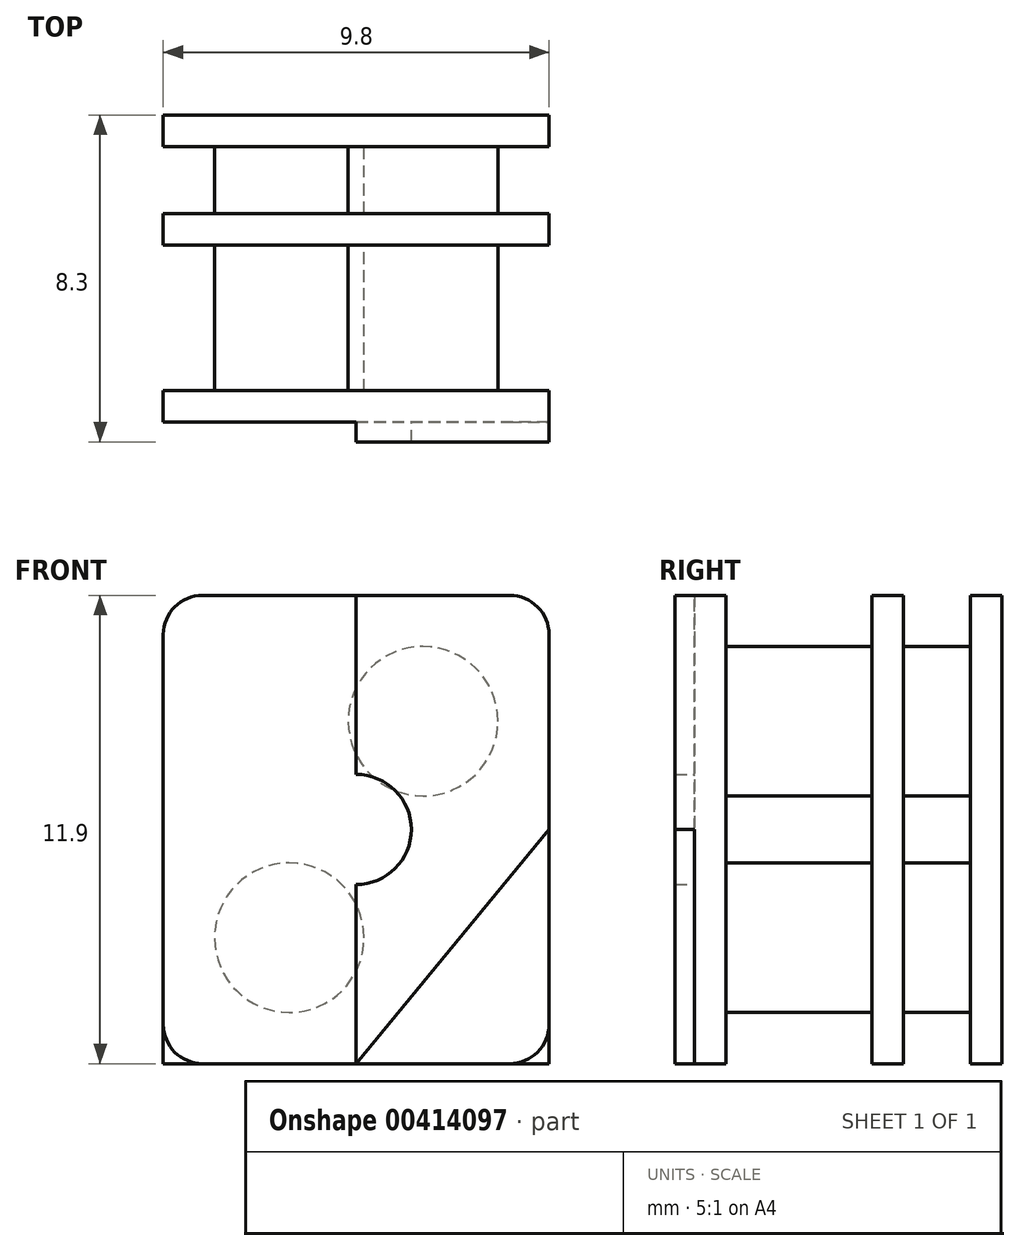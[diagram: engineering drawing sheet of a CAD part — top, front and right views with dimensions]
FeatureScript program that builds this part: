
annotation { "Feature Type Name" : "Feature", "Feature Type Description" : "" }
export const myFeature = defineFeature(function(context is Context, id is Id, definition is map)
    precondition{}
    {
        {
            var Q0;
            Q0=qCreatedBy(makeId("Front.planeOp"),FACE);
            var sketch = newSketch(context, id + "F0", { "sketchPlane" : qUnion([Q0])});
            skLineSegment(sketch, "E0.bottom", {"start": v(4.9, 5.95) * mm, "end": v(-4.9, 5.95) * mm});
            skLineSegment(sketch, "E0.top", {"start": v(4.9, -5.95) * mm, "end": v(-4.9, -5.95) * mm});
            skLineSegment(sketch, "E0.left", {"start": v(4.9, 5.95) * mm, "end": v(4.9, -5.95) * mm});
            skLineSegment(sketch, "E0.right", {"start": v(-4.9, 5.95) * mm, "end": v(-4.9, -5.95) * mm});
            skPoint(sketch, "E0.middle", {"position": v(0, 0) * mm});
            skSolve(sketch);
        }
        {
            var Q0;
            Q0=makeQuery(id+"F0.imprint","IMPRINT",FACE,{"disambiguationData":[TD([[makeQuery(id+"F0.imprint","IMPRINT",EDGE,{"derivedFrom":sQuery(id+"F0.wireOp",EDGE,"E0.bottom")}),1.0]])]});
            extrude(context, id + "F1", {"entities" : qUnion([Q0]), "depth" : .8 * mm});
        }
        {
            var Q0;
            Q0=makeQuery(id+"F1.opExtrude","CAP_FACE",FACE,{"disambiguationData":[OSD([sQuery(id+"F0.wireOp",EDGE,"E0.bottom"),sQuery(id+"F0.wireOp",EDGE,"E0.top"),sQuery(id+"F0.wireOp",EDGE,"E0.left"),sQuery(id+"F0.wireOp",EDGE,"E0.right")])],"isStart":false});
            var sketch = newSketch(context, id + "F2", { "sketchPlane" : qUnion([Q0])});
            skCircle(sketch, "E1", {"center": v(-1.7, -2.75) * mm, "radius": 1.9 * mm});
            skPoint(sketch, "E2.orphan", {"position": v(0.2, -0.85) * mm});
            skPoint(sketch, "E3.end.orphan", {"position": v(-3.6, -5.95) * mm});
            skPoint(sketch, "E4.end.orphan", {"position": v(-3.6, -4.65) * mm});
            skSolve(sketch);
        }
        {
            var Q0;
            Q0=makeQuery(id+"F1.opExtrude","CAP_FACE",FACE,{"disambiguationData":[OSD([sQuery(id+"F0.wireOp",EDGE,"E0.bottom"),sQuery(id+"F0.wireOp",EDGE,"E0.top"),sQuery(id+"F0.wireOp",EDGE,"E0.left"),sQuery(id+"F0.wireOp",EDGE,"E0.right")])],"isStart":true});
            var sketch = newSketch(context, id + "F3", { "sketchPlane" : qUnion([Q0])});
            skLineSegment(sketch, "E5.bottom", {"start": v(-4.9, 5.95) * mm, "end": v(-3.6, 5.95) * mm});
            skLineSegment(sketch, "E5.left", {"start": v(-4.9, 5.95) * mm, "end": v(-4.9, 4.65) * mm});
            skCircle(sketch, "E6", {"center": v(-1.7, 2.75) * mm, "radius": 1.9 * mm});
            skPoint(sketch, "E7.orphan", {"position": v(0.2, 0.85) * mm});
            skPoint(sketch, "E5.right.end.orphan", {"position": v(-3.6, 4.65) * mm});
            skSolve(sketch);
        }
        {
            var Q0;
            Q0=makeQuery(id+"F2.imprint","IMPRINT",FACE,{"disambiguationData":[TD([[makeQuery(id+"F2.imprint","IMPRINT",EDGE,{"derivedFrom":sQuery(id+"F2.wireOp",EDGE,"E1")}),1.0]])]});
            extrude(context, id + "F4", {"entities" : qUnion([Q0]), "operationType" : NewBodyOperationType.ADD, "depth" : 6.9 * mm});
        }
        {
            var Q0;
            Q0=makeQuery(id+"F3.imprint","IMPRINT",FACE,{"disambiguationData":[TD([[makeQuery(id+"F3.imprint","IMPRINT",EDGE,{"derivedFrom":sQuery(id+"F3.wireOp",EDGE,"E6")}),1.0]])]});
            extrude(context, id + "F5", {"entities" : qUnion([Q0]), "operationType" : NewBodyOperationType.ADD, "oppositeDirection" : true, "depth" : (.8 + 6.9) * mm});
        }
        {
            var Q0;
            Q0=makeQuery(id+"F1.opExtrude","CAP_FACE",FACE,{"disambiguationData":[OSD([sQuery(id+"F0.wireOp",EDGE,"E0.bottom"),sQuery(id+"F0.wireOp",EDGE,"E0.top"),sQuery(id+"F0.wireOp",EDGE,"E0.left"),sQuery(id+"F0.wireOp",EDGE,"E0.right")])],"isStart":false});
            var sketch = newSketch(context, id + "F6", { "sketchPlane" : qUnion([Q0])});
            skLineSegment(sketch, "E8.bottom", {"start": v(-4.9, -5.95) * mm, "end": v(4.9, -5.95) * mm});
            skLineSegment(sketch, "E8.top", {"start": v(-4.9, -5.42) * mm, "end": v(4.9, -5.42) * mm});
            skLineSegment(sketch, "E8.left", {"start": v(-4.9, -5.95) * mm, "end": v(-4.9, -5.42) * mm});
            skLineSegment(sketch, "E8.right", {"start": v(4.9, -5.95) * mm, "end": v(4.9, -5.42) * mm});
            skSolve(sketch);
        }
        {
            var Q0;
            Q0=makeQuery(id+"F6.imprint","IMPRINT",FACE,{"disambiguationData":[TD([[makeQuery(id+"F6.imprint","IMPRINT",EDGE,{"derivedFrom":sQuery(id+"F6.wireOp",EDGE,"E8.bottom")}),-1.0]])]});
            extrude(context, id + "F7", {"entities" : qUnion([Q0]), "operationType" : NewBodyOperationType.ADD, "depth" : 25.4 * mm});
        }
        {
            var Q0;
            Q0=makeQuery(id+"F7.opExtrude","SWEPT_FACE",FACE,{"disambiguationData":[OSD([sQuery(id+"F6.wireOp",EDGE,"E8.top")])]});
            var sketch = newSketch(context, id + "F8", { "sketchPlane" : qUnion([Q0])});
            skLineSegment(sketch, "E9.bottom", {"start": v(4.9, -0.8) * mm, "end": v(-4.9, -0.8) * mm});
            skLineSegment(sketch, "E9.top", {"start": v(4.9, -2.5) * mm, "end": v(-4.9, -2.5) * mm});
            skLineSegment(sketch, "E9.left", {"start": v(4.9, -0.8) * mm, "end": v(4.9, -2.5) * mm});
            skLineSegment(sketch, "E9.right", {"start": v(-4.9, -0.8) * mm, "end": v(-4.9, -2.5) * mm});
            skLineSegment(sketch, "E10.top", {"start": v(4.9, -3.3) * mm, "end": v(-4.9, -3.3) * mm});
            skLineSegment(sketch, "E10.left", {"start": v(4.9, -2.5) * mm, "end": v(4.9, -3.3) * mm});
            skLineSegment(sketch, "E10.right", {"start": v(-4.9, -2.5) * mm, "end": v(-4.9, -3.3) * mm});
            skLineSegment(sketch, "E11.top", {"start": v(4.9, -7) * mm, "end": v(-4.9, -7) * mm});
            skLineSegment(sketch, "E11.left", {"start": v(4.9, -3.3) * mm, "end": v(4.9, -7) * mm});
            skLineSegment(sketch, "E11.right", {"start": v(-4.9, -3.3) * mm, "end": v(-4.9, -7) * mm});
            skLineSegment(sketch, "E12.top", {"start": v(4.9, -7.8) * mm, "end": v(-4.9, -7.8) * mm});
            skLineSegment(sketch, "E12.left", {"start": v(4.9, -7) * mm, "end": v(4.9, -7.8) * mm});
            skLineSegment(sketch, "E12.right", {"start": v(-4.9, -7) * mm, "end": v(-4.9, -7.8) * mm});
            skSolve(sketch);
        }
        {
            var Q0;
            Q0=makeQuery(id+"F8.imprint","IMPRINT",FACE,{"disambiguationData":[TD([[makeQuery(id+"F8.imprint","IMPRINT",EDGE,{"derivedFrom":sQuery(id+"F8.wireOp",EDGE,"E9.top")}),1.0]])]});
            var Q1;
            Q1=makeQuery(id+"F8.imprint","IMPRINT",FACE,{"disambiguationData":[TD([[makeQuery(id+"F8.imprint","IMPRINT",EDGE,{"derivedFrom":sQuery(id+"F8.wireOp",EDGE,"E11.top")}),1.0]])]});
            extrude(context, id + "F9", {"entities" : qUnion([Q0, Q1]), "operationType" : NewBodyOperationType.ADD, "depth" : 11.37 * mm});
        }
        {
            var Q0;
            {var subQ2=sQuery(id+"F6.wireOp",EDGE,"E8.top");Q0=makeQuery(id+"F9.boolean.opBoolean","SPLIT",FACE,{"disambiguationData":[TD([makeQuery(id+"F9.opExtrude","SWEPT_FACE",FACE,{"disambiguationData":[OSD([sQuery(id+"F8.wireOp",EDGE,"E12.top")])]})])],"derivedFrom":makeQuery(id+"F7.opExtrude","SWEPT_FACE",FACE,{"disambiguationData":[OSD([subQ2])]})});}
            var Q1;
            Q1=makeQuery(id+"F9.boolean.opBoolean","SPLIT",FACE,{"disambiguationData":[TD([makeQuery(id+"F9.opExtrude","SWEPT_FACE",FACE,{"disambiguationData":[OSD([sQuery(id+"F8.wireOp",EDGE,"E10.top")])]})])],"derivedFrom":makeQuery(id+"F7.opExtrude","SWEPT_FACE",FACE,{"disambiguationData":[OSD([sQuery(id+"F6.wireOp",EDGE,"E8.top")])]})});
            var Q2;
            Q2=makeQuery(id+"F9.boolean.opBoolean","SPLIT",FACE,{"disambiguationData":[TD([makeQuery(id+"F9.opExtrude","SWEPT_FACE",FACE,{"disambiguationData":[OSD([sQuery(id+"F8.wireOp",EDGE,"E9.top")])]})])],"derivedFrom":makeQuery(id+"F7.opExtrude","SWEPT_FACE",FACE,{"disambiguationData":[OSD([sQuery(id+"F6.wireOp",EDGE,"E8.top")])]})});
            extrude(context, id + "F10", {"entities" : qUnion([Q0, Q1, Q2]), "operationType" : NewBodyOperationType.REMOVE, "oppositeDirection" : true, "depth" : 25.4 * mm});
        }
        {
            var Q0;
            Q0=makeQuery(id+"F9.opExtrude","CAP_EDGE",EDGE,{"disambiguationData":[OSD([sQuery(id+"F8.wireOp",EDGE,"E12.right")])],"isStart":false});
            var Q1;
            Q1=makeQuery(id+"F9.opExtrude","CAP_EDGE",EDGE,{"disambiguationData":[OSD([sQuery(id+"F8.wireOp",EDGE,"E10.right")])],"isStart":false});
            var Q2;
            Q2=makeQuery(id+"F1.opExtrude","SWEPT_EDGE",EDGE,{"disambiguationData":[OSD([sQuery(id+"F0.wireOp",EDGE,"E0.bottom"),sQuery(id+"F0.wireOp",EDGE,"E0.right")])]});
            var Q3;
            {var subQ0=sQuery(id+"F0.wireOp",EDGE,"E0.right");var subQ1=sQuery(id+"F0.wireOp",EDGE,"E0.top");var subQ2=sQuery(id+"F6.wireOp",EDGE,"E8.top");var subQ5=sQuery(id+"F6.wireOp",EDGE,"E8.bottom");var subQ6=sQuery(id+"F6.wireOp",EDGE,"E8.left");Q3=makeQuery(id+"F10.boolean.opBoolean","SPLIT",EDGE,{"disambiguationData":[TD([makeQuery(id+"F10.opExtrude","SWEPT_FACE",FACE,{"disambiguationData":[OSD([subQ2]),TDD([makeQuery(id+"F7.opExtrude","CAP_EDGE",EDGE,{"disambiguationData":[OSD([subQ2])],"isStart":true})])]})])],"derivedFrom":makeQuery(id+"F7.boolean.opBoolean","MERGE",EDGE,{"derivedFrom":[makeQuery(id+"F1.opExtrude","SWEPT_EDGE",EDGE,{"disambiguationData":[OSD([subQ1,subQ0])]}),makeQuery(id+"F7.opExtrude","SWEPT_EDGE",EDGE,{"disambiguationData":[OSD([subQ5,subQ6])]})]})});}
            var Q4;
            {var subQ0=sQuery(id+"F6.wireOp",EDGE,"E8.bottom");var subQ1=sQuery(id+"F6.wireOp",EDGE,"E8.left");var subQ2=sQuery(id+"F8.wireOp",EDGE,"E9.top");var subQ3=sQuery(id+"F0.wireOp",EDGE,"E0.right");var subQ5=sQuery(id+"F0.wireOp",EDGE,"E0.top");Q4=makeQuery(id+"F10.boolean.opBoolean","SPLIT",EDGE,{"disambiguationData":[TD([makeQuery(id+"F9.opExtrude","SWEPT_FACE",FACE,{"disambiguationData":[OSD([subQ2])]})])],"derivedFrom":makeQuery(id+"F7.boolean.opBoolean","MERGE",EDGE,{"derivedFrom":[makeQuery(id+"F1.opExtrude","SWEPT_EDGE",EDGE,{"disambiguationData":[OSD([subQ5,subQ3])]}),makeQuery(id+"F7.opExtrude","SWEPT_EDGE",EDGE,{"disambiguationData":[OSD([subQ0,subQ1])]})]})});}
            var Q5;
            {var subQ0=sQuery(id+"F6.wireOp",EDGE,"E8.bottom");var subQ1=sQuery(id+"F8.wireOp",EDGE,"E11.top");var subQ2=sQuery(id+"F6.wireOp",EDGE,"E8.left");var subQ3=sQuery(id+"F0.wireOp",EDGE,"E0.right");var subQ4=sQuery(id+"F0.wireOp",EDGE,"E0.top");Q5=makeQuery(id+"F10.boolean.opBoolean","SPLIT",EDGE,{"disambiguationData":[TD([makeQuery(id+"F9.opExtrude","SWEPT_FACE",FACE,{"disambiguationData":[OSD([subQ1])]})])],"derivedFrom":makeQuery(id+"F7.boolean.opBoolean","MERGE",EDGE,{"derivedFrom":[makeQuery(id+"F1.opExtrude","SWEPT_EDGE",EDGE,{"disambiguationData":[OSD([subQ4,subQ3])]}),makeQuery(id+"F7.opExtrude","SWEPT_EDGE",EDGE,{"disambiguationData":[OSD([subQ0,subQ2])]})]})});}
            var Q6;
            Q6=makeQuery(id+"F9.opExtrude","CAP_EDGE",EDGE,{"disambiguationData":[OSD([sQuery(id+"F8.wireOp",EDGE,"E12.left")])],"isStart":false});
            var Q7;
            Q7=makeQuery(id+"F9.opExtrude","CAP_EDGE",EDGE,{"disambiguationData":[OSD([sQuery(id+"F8.wireOp",EDGE,"E10.left")])],"isStart":false});
            var Q8;
            Q8=makeQuery(id+"F1.opExtrude","SWEPT_EDGE",EDGE,{"disambiguationData":[OSD([sQuery(id+"F0.wireOp",EDGE,"E0.bottom"),sQuery(id+"F0.wireOp",EDGE,"E0.left")])]});
            var Q9;
            {var subQ0=sQuery(id+"F0.wireOp",EDGE,"E0.left");var subQ1=sQuery(id+"F0.wireOp",EDGE,"E0.top");var subQ2=sQuery(id+"F6.wireOp",EDGE,"E8.top");var subQ5=sQuery(id+"F6.wireOp",EDGE,"E8.bottom");var subQ6=sQuery(id+"F6.wireOp",EDGE,"E8.right");Q9=makeQuery(id+"F10.boolean.opBoolean","SPLIT",EDGE,{"disambiguationData":[TD([makeQuery(id+"F10.opExtrude","SWEPT_FACE",FACE,{"disambiguationData":[OSD([subQ2]),TDD([makeQuery(id+"F7.opExtrude","CAP_EDGE",EDGE,{"disambiguationData":[OSD([subQ2])],"isStart":true})])]})])],"derivedFrom":makeQuery(id+"F7.boolean.opBoolean","MERGE",EDGE,{"derivedFrom":[makeQuery(id+"F1.opExtrude","SWEPT_EDGE",EDGE,{"disambiguationData":[OSD([subQ1,subQ0])]}),makeQuery(id+"F7.opExtrude","SWEPT_EDGE",EDGE,{"disambiguationData":[OSD([subQ5,subQ6])]})]})});}
            var Q10;
            {var subQ0=sQuery(id+"F6.wireOp",EDGE,"E8.right");var subQ1=sQuery(id+"F8.wireOp",EDGE,"E9.top");var subQ3=sQuery(id+"F6.wireOp",EDGE,"E8.bottom");var subQ4=sQuery(id+"F0.wireOp",EDGE,"E0.left");var subQ5=sQuery(id+"F0.wireOp",EDGE,"E0.top");Q10=makeQuery(id+"F10.boolean.opBoolean","SPLIT",EDGE,{"disambiguationData":[TD([makeQuery(id+"F9.opExtrude","SWEPT_FACE",FACE,{"disambiguationData":[OSD([subQ1])]})])],"derivedFrom":makeQuery(id+"F7.boolean.opBoolean","MERGE",EDGE,{"derivedFrom":[makeQuery(id+"F1.opExtrude","SWEPT_EDGE",EDGE,{"disambiguationData":[OSD([subQ5,subQ4])]}),makeQuery(id+"F7.opExtrude","SWEPT_EDGE",EDGE,{"disambiguationData":[OSD([subQ3,subQ0])]})]})});}
            var Q11;
            {var subQ0=sQuery(id+"F6.wireOp",EDGE,"E8.right");var subQ1=sQuery(id+"F6.wireOp",EDGE,"E8.bottom");var subQ2=sQuery(id+"F8.wireOp",EDGE,"E11.top");var subQ3=sQuery(id+"F0.wireOp",EDGE,"E0.left");var subQ4=sQuery(id+"F0.wireOp",EDGE,"E0.top");Q11=makeQuery(id+"F10.boolean.opBoolean","SPLIT",EDGE,{"disambiguationData":[TD([makeQuery(id+"F9.opExtrude","SWEPT_FACE",FACE,{"disambiguationData":[OSD([subQ2])]})])],"derivedFrom":makeQuery(id+"F7.boolean.opBoolean","MERGE",EDGE,{"derivedFrom":[makeQuery(id+"F1.opExtrude","SWEPT_EDGE",EDGE,{"disambiguationData":[OSD([subQ4,subQ3])]}),makeQuery(id+"F7.opExtrude","SWEPT_EDGE",EDGE,{"disambiguationData":[OSD([subQ1,subQ0])]})]})});}
            fillet(context, id + "F11", {"entities" : qUnion([Q0, Q1, Q2, Q3, Q4, Q5, Q6, Q7, Q8, Q9, Q10, Q11]), "radius" : 1 * mm, "tangentPropagation" : true, "allowEdgeOverflow" : false});
        }
        {
            var Q0;
            {var subQ0=sQuery(id+"F8.wireOp",EDGE,"E12.top");Q0=makeQuery(id+"F10.boolean.opBoolean","MERGE",FACE,{"derivedFrom":[makeQuery(id+"F9.opExtrude","SWEPT_FACE",FACE,{"disambiguationData":[OSD([subQ0])]}),makeQuery(id+"F10.opExtrude","SWEPT_FACE",FACE,{"disambiguationData":[OSD([subQ0])]})]});}
            var sketch = newSketch(context, id + "F12", { "sketchPlane" : qUnion([Q0])});
            skLineSegment(sketch, "E13", {"start": v(-4.9, 0) * mm, "end": v(4.9, 0) * mm});
            skLineSegment(sketch, "E14", {"start": v(4.9, 0) * mm, "end": v(0, -5.95) * mm});
            skLineSegment(sketch, "E15", {"start": v(0, -5.95) * mm, "end": v(0, 5.95) * mm});
            skCircle(sketch, "E16", {"center": v(0, 0) * mm, "radius": 1.95 * mm});
            skCircle(sketch, "E17", {"center": v(0, 0) * mm, "radius": 1.4 * mm});
            skSolve(sketch);
        }
        {
            var Q0;
            {var subQ0=sQuery(id+"F12.wireOp",EDGE,"E16");var subQ1=sQuery(id+"F12.wireOp",EDGE,"E13");var subQ2=makeQuery(id+"F12.imprint","INTERSECT",VERTEX,{"disambiguationData":[OD(0.0)],"derivedFrom":[subQ1,subQ0]});Q0=makeQuery(id+"F12.imprint","IMPRINT",FACE,{"disambiguationData":[TD([[makeQuery(id+"F12.imprint","IMPRINT",EDGE,{"disambiguationData":[TD([[subQ2,-1.0]])],"derivedFrom":subQ1}),-1.0]])]});}
            var Q1;
            {var subQ0=sQuery(id+"F12.wireOp",EDGE,"E17");var subQ1=sQuery(id+"F12.wireOp",EDGE,"E13");var subQ2=makeQuery(id+"F12.imprint","INTERSECT",VERTEX,{"disambiguationData":[OD(1.0)],"derivedFrom":[subQ1,subQ0]});Q1=makeQuery(id+"F12.imprint","IMPRINT",FACE,{"disambiguationData":[TD([[makeQuery(id+"F12.imprint","IMPRINT",EDGE,{"disambiguationData":[TD([[subQ2,-1.0]])],"derivedFrom":subQ1}),1.0]])]});}
            var Q2;
            {var subQ0=sQuery(id+"F12.wireOp",EDGE,"E16");var subQ1=sQuery(id+"F12.wireOp",EDGE,"E13");var subQ2=makeQuery(id+"F12.imprint","INTERSECT",VERTEX,{"disambiguationData":[OD(0.0)],"derivedFrom":[subQ1,subQ0]});Q2=makeQuery(id+"F12.imprint","IMPRINT",FACE,{"disambiguationData":[TD([[makeQuery(id+"F12.imprint","IMPRINT",EDGE,{"disambiguationData":[TD([[subQ2,-1.0]])],"derivedFrom":subQ1}),1.0]])]});}
            var Q3;
            {var subQ0=sQuery(id+"F12.wireOp",EDGE,"E17");var subQ1=sQuery(id+"F12.wireOp",EDGE,"E13");var subQ2=makeQuery(id+"F12.imprint","INTERSECT",VERTEX,{"disambiguationData":[OD(1.0)],"derivedFrom":[subQ1,subQ0]});Q3=makeQuery(id+"F12.imprint","IMPRINT",FACE,{"disambiguationData":[TD([[makeQuery(id+"F12.imprint","IMPRINT",EDGE,{"disambiguationData":[TD([[subQ2,-1.0]])],"derivedFrom":subQ1}),-1.0]])]});}
            extrude(context, id + "F13", {"entities" : qUnion([Q0, Q1, Q2, Q3]), "operationType" : NewBodyOperationType.ADD, "depth" : .5 * mm});
        }
    });
